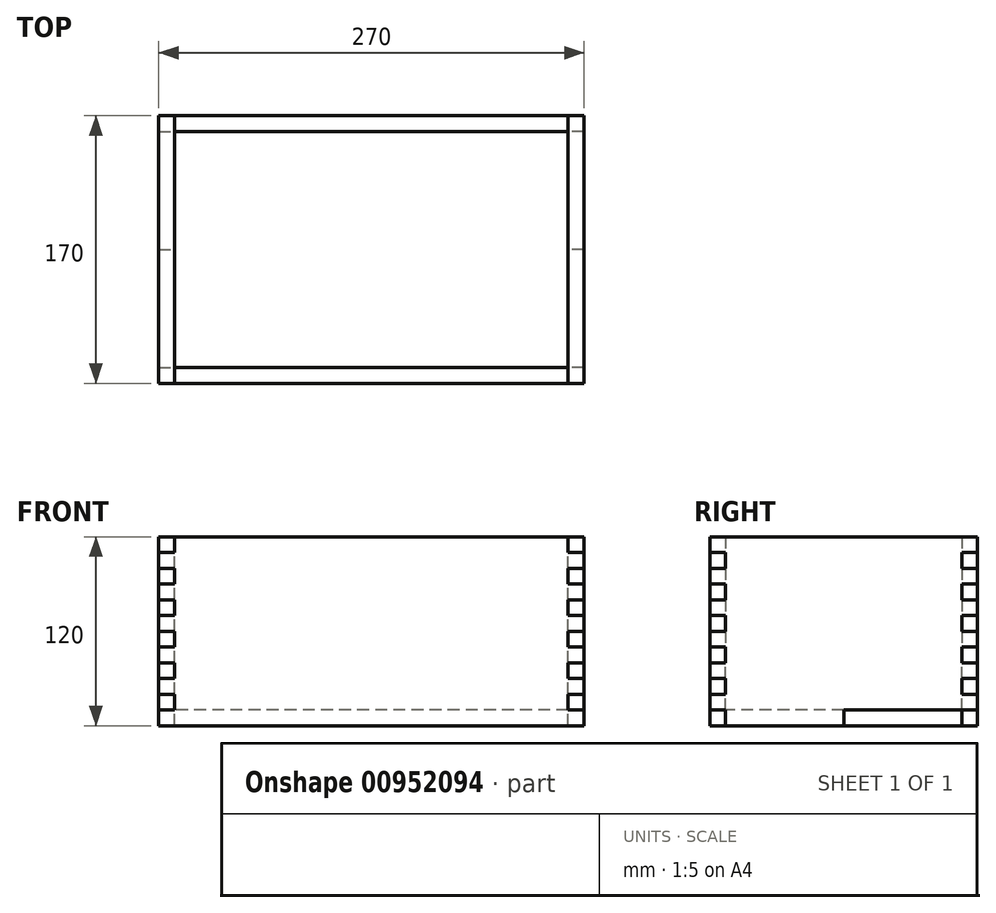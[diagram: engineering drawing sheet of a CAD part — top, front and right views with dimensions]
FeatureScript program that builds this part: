
annotation { "Feature Type Name" : "Feature", "Feature Type Description" : "" }
export const myFeature = defineFeature(function(context is Context, id is Id, definition is map)
    precondition{}
    {
        {
            var Q0;
            Q0=qCreatedBy(makeId("Top.planeOp"),FACE);
            var sketch = newSketch(context, id + "F0", { "sketchPlane" : qUnion([Q0])});
            skLineSegment(sketch, "E0.bottom", {"start": v(125, 75) * mm, "end": v(-125, 75) * mm});
            skLineSegment(sketch, "E0.top", {"start": v(125, -75) * mm, "end": v(-125, -75) * mm});
            skLineSegment(sketch, "E0.left", {"start": v(125, 75) * mm, "end": v(125, -75) * mm});
            skLineSegment(sketch, "E0.right", {"start": v(-125, 75) * mm, "end": v(-125, -75) * mm});
            skPoint(sketch, "E0.middle", {"position": v(0, 0) * mm});
            skSolve(sketch);
        }
        {
            var Q0;
            Q0 = qSketchRegion(id + "F0", true);
            extrude(context, id + "F1", {"entities" : qUnion([Q0]), "depth" : 10 * mm, "offsetDistance" : 25 * mm});
        }
        {
            var Q0;
            Q0=makeQuery(id+"F1.opExtrude","SWEPT_FACE",FACE,{"disambiguationData":[OSD([sQuery(id+"F0.wireOp",EDGE,"E0.right")])]});
            var sketch = newSketch(context, id + "F2", { "sketchPlane" : qUnion([Q0])});
            skLineSegment(sketch, "E1.bottom", {"start": v(0, 0) * mm, "end": v(75, 0) * mm});
            skLineSegment(sketch, "E1.right", {"start": v(85, 10) * mm, "end": v(85, 20) * mm});
            skLineSegment(sketch, "E2.0", {"start": v(75, 0) * mm, "end": v(75, 10) * mm});
            skLineSegment(sketch, "E3", {"start": v(85, 10) * mm, "end": v(75, 10) * mm});
            skLineSegment(sketch, "E4.0.1.0", {"start": v(85, 20) * mm, "end": v(75, 20) * mm});
            skLineSegment(sketch, "E4.0.2.0", {"start": v(85, 30) * mm, "end": v(75, 30) * mm});
            skLineSegment(sketch, "E4.0.3.0", {"start": v(85, 40) * mm, "end": v(75, 40) * mm});
            skLineSegment(sketch, "E4.0.4.0", {"start": v(85, 50) * mm, "end": v(75, 50) * mm});
            skLineSegment(sketch, "E4.0.5.0", {"start": v(85, 60) * mm, "end": v(75, 60) * mm});
            skLineSegment(sketch, "E4.0.6.0", {"start": v(85, 70) * mm, "end": v(75, 70) * mm});
            skLineSegment(sketch, "E4.0.7.0", {"start": v(85, 80) * mm, "end": v(75, 80) * mm});
            skLineSegment(sketch, "E4.0.8.0", {"start": v(85, 90) * mm, "end": v(75, 90) * mm});
            skLineSegment(sketch, "E4.0.9.0", {"start": v(85, 100) * mm, "end": v(75, 100) * mm});
            skLineSegment(sketch, "E4.0.10.0", {"start": v(85, 110) * mm, "end": v(75, 110) * mm});
            skLineSegment(sketch, "E4.0.11.0", {"start": v(85, 120) * mm, "end": v(75, 120) * mm});
            skLineSegment(sketch, "E4.direction1", {"start": v(75, 10) * mm, "end": v(100, 10) * mm, "construction": true});
            skLineSegment(sketch, "E5.trimOffspring", {"start": v(75, 20) * mm, "end": v(75, 30) * mm});
            skLineSegment(sketch, "E6.trimOffspring", {"start": v(85, 30) * mm, "end": v(85, 40) * mm});
            skLineSegment(sketch, "E7.trimOffspring", {"start": v(75, 40) * mm, "end": v(75, 50) * mm});
            skLineSegment(sketch, "E8.trimOffspring", {"start": v(85, 50) * mm, "end": v(85, 60) * mm});
            skLineSegment(sketch, "E9.trimOffspring", {"start": v(75, 60) * mm, "end": v(75, 70) * mm});
            skLineSegment(sketch, "E10.trimOffspring", {"start": v(85, 70) * mm, "end": v(85, 80) * mm});
            skLineSegment(sketch, "E11.trimOffspring", {"start": v(75, 80) * mm, "end": v(75, 90) * mm});
            skLineSegment(sketch, "E12.trimOffspring", {"start": v(85, 90) * mm, "end": v(85, 100) * mm});
            skLineSegment(sketch, "E13.trimOffspring", {"start": v(75, 100) * mm, "end": v(75, 110) * mm});
            skLineSegment(sketch, "E14.trimOffspring", {"start": v(85, 110) * mm, "end": v(85, 120) * mm});
            skLineSegment(sketch, "E15", {"start": v(0, 0) * mm, "end": v(0, 119.51) * mm});
            skLineSegment(sketch, "E16.MirrorCS", {"start": v(-85, 10) * mm, "end": v(-75, 10) * mm});
            skLineSegment(sketch, "E17.MirrorCS", {"start": v(-85, 30) * mm, "end": v(-75, 30) * mm});
            skLineSegment(sketch, "E18.MirrorCS", {"start": v(-85, 110) * mm, "end": v(-75, 110) * mm});
            skLineSegment(sketch, "E19.MirrorCS", {"start": v(-85, 20) * mm, "end": v(-75, 20) * mm});
            skLineSegment(sketch, "E20.MirrorCS", {"start": v(-85, 80) * mm, "end": v(-75, 80) * mm});
            skLineSegment(sketch, "E21.MirrorCS", {"start": v(-75, 60) * mm, "end": v(-75, 70) * mm});
            skLineSegment(sketch, "E22.MirrorCS", {"start": v(-85, 30) * mm, "end": v(-85, 40) * mm});
            skLineSegment(sketch, "E23.MirrorCS", {"start": v(-75, 10) * mm, "end": v(-100, 10) * mm, "construction": true});
            skLineSegment(sketch, "E24.MirrorCS", {"start": v(-85, 50) * mm, "end": v(-75, 50) * mm});
            skLineSegment(sketch, "E25.MirrorCS", {"start": v(-85, 100) * mm, "end": v(-75, 100) * mm});
            skLineSegment(sketch, "E26.MirrorCS", {"start": v(-85, 120) * mm, "end": v(-75, 120) * mm});
            skLineSegment(sketch, "E27.MirrorCS", {"start": v(-85, 90) * mm, "end": v(-75, 90) * mm});
            skLineSegment(sketch, "E28.MirrorCS", {"start": v(-75, 100) * mm, "end": v(-75, 110) * mm});
            skLineSegment(sketch, "E29.MirrorCS", {"start": v(-85, 40) * mm, "end": v(-75, 40) * mm});
            skLineSegment(sketch, "E30.MirrorCS", {"start": v(-85, 110) * mm, "end": v(-85, 120) * mm});
            skLineSegment(sketch, "E31.MirrorCS", {"start": v(-75, 0) * mm, "end": v(-75, 10) * mm});
            skLineSegment(sketch, "E32.MirrorCS", {"start": v(-75, 40) * mm, "end": v(-75, 50) * mm});
            skLineSegment(sketch, "E33.MirrorCS", {"start": v(-75, 80) * mm, "end": v(-75, 90) * mm});
            skLineSegment(sketch, "E34.MirrorCS", {"start": v(-85, 70) * mm, "end": v(-75, 70) * mm});
            skLineSegment(sketch, "E35.MirrorCS", {"start": v(-85, 70) * mm, "end": v(-85, 80) * mm});
            skLineSegment(sketch, "E36.MirrorCS", {"start": v(-75, 20) * mm, "end": v(-75, 30) * mm});
            skLineSegment(sketch, "E37.MirrorCS", {"start": v(-85, 60) * mm, "end": v(-75, 60) * mm});
            skLineSegment(sketch, "E38.MirrorCS", {"start": v(-85, 90) * mm, "end": v(-85, 100) * mm});
            skLineSegment(sketch, "E39.MirrorCS", {"start": v(-85, 50) * mm, "end": v(-85, 60) * mm});
            skLineSegment(sketch, "E40.MirrorCS", {"start": v(0, 0) * mm, "end": v(-75, 0) * mm});
            skLineSegment(sketch, "E41.MirrorCS", {"start": v(-85, 10) * mm, "end": v(-85, 20) * mm});
            skLineSegment(sketch, "E42", {"start": v(-75, 10) * mm, "end": v(-75, 0) * mm});
            skLineSegment(sketch, "E43", {"start": v(-75, 0) * mm, "end": v(75, 0) * mm});
            skLineSegment(sketch, "E44", {"start": v(75, 120) * mm, "end": v(-75, 120) * mm});
            skSolve(sketch);
        }
        {
            var Q0;
            {var subQ0=sQuery(id+"F2.wireOp",EDGE,"E16.MirrorCS");Q0=makeQuery(id+"F2.imprint","IMPRINT",FACE,{"disambiguationData":[TD([[makeQuery(id+"F2.imprint","IMPRINT",EDGE,{"derivedFrom":subQ0}),1.0]])]});}
            var Q1;
            {var subQ4=sQuery(id+"F2.wireOp",EDGE,"E1.top");Q1=makeQuery(id+"F2.imprint","IMPRINT",FACE,{"disambiguationData":[TD([[makeQuery(id+"F2.imprint","IMPRINT",EDGE,{"derivedFrom":subQ4}),-1.0]])]});}
            var Q2;
            {var subQ5=sQuery(id+"F2.wireOp",EDGE,"E42");Q2=makeQuery(id+"F2.imprint","IMPRINT",FACE,{"disambiguationData":[TD([[makeQuery(id+"F2.imprint","IMPRINT",EDGE,{"derivedFrom":subQ5}),1.0]])]});}
            var Q3;
            {var subQ5=sQuery(id+"F2.wireOp",EDGE,"E2.0");Q3=makeQuery(id+"F2.imprint","IMPRINT",FACE,{"disambiguationData":[TD([[makeQuery(id+"F2.imprint","IMPRINT",EDGE,{"derivedFrom":subQ5}),-1.0]])]});}
            extrude(context, id + "F3", {"entities" : qUnion([Q0, Q1, Q2, Q3]), "depth" : 10 * mm, "offsetDistance" : 25 * mm});
        }
        {
            var Q0;
            Q0=makeQuery(id+"F3.opExtrude","SWEPT_BODY",BODY,{"disambiguationData":[OSD([sQuery(id+"F2.wireOp",EDGE,"E1.top"),sQuery(id+"F2.wireOp",EDGE,"E1.right"),sQuery(id+"F2.wireOp",EDGE,"E3"),sQuery(id+"F2.wireOp",EDGE,"E4.0.1.0"),sQuery(id+"F2.wireOp",EDGE,"E4.0.2.0"),sQuery(id+"F2.wireOp",EDGE,"E4.0.3.0"),sQuery(id+"F2.wireOp",EDGE,"E4.0.4.0"),sQuery(id+"F2.wireOp",EDGE,"E4.0.5.0"),sQuery(id+"F2.wireOp",EDGE,"E4.0.6.0"),sQuery(id+"F2.wireOp",EDGE,"E4.0.7.0"),sQuery(id+"F2.wireOp",EDGE,"E4.0.8.0"),sQuery(id+"F2.wireOp",EDGE,"E4.0.9.0"),sQuery(id+"F2.wireOp",EDGE,"E4.0.10.0"),sQuery(id+"F2.wireOp",EDGE,"E4.0.11.0"),sQuery(id+"F2.wireOp",EDGE,"E4.0.12.0"),sQuery(id+"F2.wireOp",EDGE,"537c9ae5-ac88-4067-9cdc-c8666f4d1ff7.0.0.13"),sQuery(id+"F2.wireOp",EDGE,"E5.trimOffspring"),sQuery(id+"F2.wireOp",EDGE,"E6.trimOffspring"),sQuery(id+"F2.wireOp",EDGE,"E7.trimOffspring"),sQuery(id+"F2.wireOp",EDGE,"E8.trimOffspring"),sQuery(id+"F2.wireOp",EDGE,"E9.trimOffspring"),sQuery(id+"F2.wireOp",EDGE,"E10.trimOffspring"),sQuery(id+"F2.wireOp",EDGE,"E11.trimOffspring"),sQuery(id+"F2.wireOp",EDGE,"E12.trimOffspring"),sQuery(id+"F2.wireOp",EDGE,"E13.trimOffspring"),sQuery(id+"F2.wireOp",EDGE,"E14.trimOffspring"),sQuery(id+"F2.wireOp",EDGE,"0b9fcc7d-6960-4033-8808-0068f41279c2.trimOffspring"),sQuery(id+"F2.wireOp",EDGE,"4482ad7b-3059-4b9f-bfc4-0e486806ed4d.trimOffspring"),sQuery(id+"F2.wireOp",EDGE,"a6469687-5e93-42e0-971b-389a09a8f158.trimOffspring"),sQuery(id+"F2.wireOp",EDGE,"E16.MirrorCS"),sQuery(id+"F2.wireOp",EDGE,"E17.MirrorCS"),sQuery(id+"F2.wireOp",EDGE,"e481a68e-a1f5-484a-a6b3-999f8e45b44d3.MirrorCS"),sQuery(id+"F2.wireOp",EDGE,"E18.MirrorCS"),sQuery(id+"F2.wireOp",EDGE,"E19.MirrorCS"),sQuery(id+"F2.wireOp",EDGE,"E20.MirrorCS"),sQuery(id+"F2.wireOp",EDGE,"E21.MirrorCS"),sQuery(id+"F2.wireOp",EDGE,"E22.MirrorCS"),sQuery(id+"F2.wireOp",EDGE,"e481a68e-a1f5-484a-a6b3-999f8e45b44d9.MirrorCS"),sQuery(id+"F2.wireOp",EDGE,"E24.MirrorCS"),sQuery(id+"F2.wireOp",EDGE,"e481a68e-a1f5-484a-a6b3-999f8e45b44d12.MirrorCS"),sQuery(id+"F2.wireOp",EDGE,"E25.MirrorCS"),sQuery(id+"F2.wireOp",EDGE,"E26.MirrorCS"),sQuery(id+"F2.wireOp",EDGE,"E27.MirrorCS"),sQuery(id+"F2.wireOp",EDGE,"E28.MirrorCS"),sQuery(id+"F2.wireOp",EDGE,"E29.MirrorCS"),sQuery(id+"F2.wireOp",EDGE,"e481a68e-a1f5-484a-a6b3-999f8e45b44d18.MirrorCS"),sQuery(id+"F2.wireOp",EDGE,"E30.MirrorCS"),sQuery(id+"F2.wireOp",EDGE,"E32.MirrorCS"),sQuery(id+"F2.wireOp",EDGE,"E33.MirrorCS"),sQuery(id+"F2.wireOp",EDGE,"E34.MirrorCS"),sQuery(id+"F2.wireOp",EDGE,"E35.MirrorCS"),sQuery(id+"F2.wireOp",EDGE,"E36.MirrorCS"),sQuery(id+"F2.wireOp",EDGE,"E37.MirrorCS"),sQuery(id+"F2.wireOp",EDGE,"E38.MirrorCS"),sQuery(id+"F2.wireOp",EDGE,"E178.MirrorCS"),sQuery(id+"F2.wireOp",EDGE,"E39.MirrorCS"),sQuery(id+"F2.wireOp",EDGE,"E41.MirrorCS"),sQuery(id+"F2.wireOp",EDGE,"e481a68e-a1f5-484a-a6b3-999f8e45b44d32.MirrorCS"),sQuery(id+"F2.wireOp",EDGE,"E42"),sQuery(id+"F2.wireOp",EDGE,"E43"),sQuery(id+"F2.wireOp",EDGE,"E2.0")])]});
            var Q1;
            Q1=qCreatedBy(makeId("Right.planeOp"),FACE);
            mirror(context, id + "F4", {"entities" : qUnion([Q0]), "mirrorPlane" : qUnion([Q1])});
        }
        {
            var Q0;
            Q0=makeQuery(id+"F1.opExtrude","SWEPT_FACE",FACE,{"disambiguationData":[OSD([sQuery(id+"F0.wireOp",EDGE,"E0.bottom")])]});
            var sketch = newSketch(context, id + "F5", { "sketchPlane" : qUnion([Q0])});
            skLineSegment(sketch, "E45", {"start": v(0, 0) * mm, "end": v(135, 0) * mm});
            skLineSegment(sketch, "E46", {"start": v(135, 0) * mm, "end": v(135, 10) * mm});
            skLineSegment(sketch, "E47", {"start": v(135, 10) * mm, "end": v(125, 10) * mm});
            skLineSegment(sketch, "E48", {"start": v(125, 10) * mm, "end": v(125, 20) * mm});
            skLineSegment(sketch, "E49", {"start": v(125, 20) * mm, "end": v(135, 20) * mm});
            skLineSegment(sketch, "E50", {"start": v(135, 20) * mm, "end": v(135, 30) * mm});
            skLineSegment(sketch, "E51", {"start": v(135, 30) * mm, "end": v(125, 30) * mm});
            skLineSegment(sketch, "E52", {"start": v(125, 30) * mm, "end": v(125, 40) * mm});
            skLineSegment(sketch, "E53", {"start": v(125, 40) * mm, "end": v(135, 40) * mm});
            skLineSegment(sketch, "E54.0.1.0", {"start": v(125, 50) * mm, "end": v(135, 50) * mm});
            skLineSegment(sketch, "E54.0.2.0", {"start": v(125, 60) * mm, "end": v(135, 60) * mm});
            skLineSegment(sketch, "E54.0.3.0", {"start": v(125, 70) * mm, "end": v(135, 70) * mm});
            skLineSegment(sketch, "E54.0.4.0", {"start": v(125, 80) * mm, "end": v(135, 80) * mm});
            skLineSegment(sketch, "E54.0.5.0", {"start": v(125, 90) * mm, "end": v(135, 90) * mm});
            skLineSegment(sketch, "E54.0.6.0", {"start": v(125, 100) * mm, "end": v(135, 100) * mm});
            skLineSegment(sketch, "E54.0.7.0", {"start": v(125, 110) * mm, "end": v(135, 110) * mm});
            skLineSegment(sketch, "E54.0.8.0", {"start": v(125, 120) * mm, "end": v(135, 120) * mm});
            skLineSegment(sketch, "E54.direction1", {"start": v(125, 40) * mm, "end": v(150, 40) * mm, "construction": true});
            skLineSegment(sketch, "E54.direction2", {"start": v(125, 40) * mm, "end": v(125, 50) * mm, "construction": true});
            skLineSegment(sketch, "E55", {"start": v(135, 50) * mm, "end": v(135, 40) * mm});
            skLineSegment(sketch, "E56", {"start": v(125, 60) * mm, "end": v(125, 50) * mm});
            skLineSegment(sketch, "E57", {"start": v(135, 70) * mm, "end": v(135, 60) * mm});
            skLineSegment(sketch, "E58", {"start": v(125, 80) * mm, "end": v(125, 70) * mm});
            skLineSegment(sketch, "E59", {"start": v(135, 90) * mm, "end": v(135, 80) * mm});
            skLineSegment(sketch, "E60", {"start": v(125, 100) * mm, "end": v(125, 90) * mm});
            skLineSegment(sketch, "E61", {"start": v(135, 110) * mm, "end": v(135, 100) * mm});
            skLineSegment(sketch, "E62", {"start": v(125, 120) * mm, "end": v(125, 110) * mm});
            skLineSegment(sketch, "E63", {"start": v(0, 120) * mm, "end": v(0, 0) * mm});
            skLineSegment(sketch, "E64.MirrorCS", {"start": v(-125, 40) * mm, "end": v(-135, 40) * mm});
            skLineSegment(sketch, "E65.MirrorCS", {"start": v(-125, 40) * mm, "end": v(-150, 40) * mm, "construction": true});
            skLineSegment(sketch, "E66.MirrorCS", {"start": v(-125, 120) * mm, "end": v(-135, 120) * mm});
            skLineSegment(sketch, "E67.MirrorCS", {"start": v(-125, 80) * mm, "end": v(-135, 80) * mm});
            skLineSegment(sketch, "E68.MirrorCS", {"start": v(-135, 30) * mm, "end": v(-125, 30) * mm});
            skLineSegment(sketch, "E69.MirrorCS", {"start": v(-125, 50) * mm, "end": v(-135, 50) * mm});
            skLineSegment(sketch, "E70.MirrorCS", {"start": v(-125, 40) * mm, "end": v(-125, 50) * mm, "construction": true});
            skLineSegment(sketch, "E71.MirrorCS", {"start": v(-135, 110) * mm, "end": v(-135, 100) * mm});
            skLineSegment(sketch, "E72.MirrorCS", {"start": v(-125, 60) * mm, "end": v(-135, 60) * mm});
            skLineSegment(sketch, "E73.MirrorCS", {"start": v(-125, 20) * mm, "end": v(-135, 20) * mm});
            skLineSegment(sketch, "E74.MirrorCS", {"start": v(-125, 110) * mm, "end": v(-135, 110) * mm});
            skLineSegment(sketch, "E75.MirrorCS", {"start": v(-135, 90) * mm, "end": v(-135, 80) * mm});
            skLineSegment(sketch, "E76.MirrorCS", {"start": v(-135, 70) * mm, "end": v(-135, 60) * mm});
            skLineSegment(sketch, "E77.MirrorCS", {"start": v(-135, 10) * mm, "end": v(-125, 10) * mm});
            skLineSegment(sketch, "E78.MirrorCS", {"start": v(-135, 0) * mm, "end": v(-135, 10) * mm});
            skLineSegment(sketch, "E79.MirrorCS", {"start": v(-125, 30) * mm, "end": v(-125, 40) * mm});
            skLineSegment(sketch, "E80.MirrorCS", {"start": v(-125, 80) * mm, "end": v(-125, 70) * mm});
            skLineSegment(sketch, "E81.MirrorCS", {"start": v(-125, 100) * mm, "end": v(-125, 90) * mm});
            skLineSegment(sketch, "E82.MirrorCS", {"start": v(-135, 50) * mm, "end": v(-135, 40) * mm});
            skLineSegment(sketch, "E83.MirrorCS", {"start": v(-125, 60) * mm, "end": v(-125, 50) * mm});
            skLineSegment(sketch, "E84.MirrorCS", {"start": v(-125, 120) * mm, "end": v(-125, 110) * mm});
            skLineSegment(sketch, "E85.MirrorCS", {"start": v(-125, 100) * mm, "end": v(-135, 100) * mm});
            skLineSegment(sketch, "E86.MirrorCS", {"start": v(-125, 90) * mm, "end": v(-135, 90) * mm});
            skLineSegment(sketch, "E87.MirrorCS", {"start": v(-125, 10) * mm, "end": v(-125, 20) * mm});
            skLineSegment(sketch, "E88.MirrorCS", {"start": v(-125, 70) * mm, "end": v(-135, 70) * mm});
            skLineSegment(sketch, "E89.MirrorCS", {"start": v(-135, 20) * mm, "end": v(-135, 30) * mm});
            skLineSegment(sketch, "E90.MirrorCS", {"start": v(0, 0) * mm, "end": v(-135, 0) * mm});
            skLineSegment(sketch, "E91", {"start": v(-125, 120) * mm, "end": v(125, 120) * mm});
            skSolve(sketch);
        }
        {
            var Q0;
            Q0=makeQuery(id+"F5.imprint","IMPRINT",FACE,{"disambiguationData":[TD([[makeQuery(id+"F5.imprint","IMPRINT",EDGE,{"derivedFrom":sQuery(id+"F5.wireOp",EDGE,"E64.MirrorCS")}),-1.0]])]});
            var Q1;
            {var subQ0=sQuery(id+"F5.wireOp",EDGE,"E48");Q1=makeQuery(id+"F5.imprint","IMPRINT",FACE,{"disambiguationData":[TD([[makeQuery(id+"F5.imprint","IMPRINT",EDGE,{"derivedFrom":subQ0}),1.0]])]});}
            var Q2;
            {var subQ3=sQuery(id+"F0.wireOp",EDGE,"E0.bottom");var subQ6=makeQuery(id+"F1.opExtrude","SWEPT_EDGE",EDGE,{"disambiguationData":[OSD([subQ3,sQuery(id+"F0.wireOp",EDGE,"E0.left")])]});Q2=makeQuery(id+"F5.imprint","IMPRINT",FACE,{"disambiguationData":[TD([[makeQuery(id+"F5.imprint","IMPRINT",EDGE,{"derivedFrom":subQ6}),1.0]])]});}
            var Q3;
            {var subQ1=sQuery(id+"F0.wireOp",EDGE,"E0.bottom");var subQ2=makeQuery(id+"F1.opExtrude","SWEPT_EDGE",EDGE,{"disambiguationData":[OSD([subQ1,sQuery(id+"F0.wireOp",EDGE,"E0.right")])]});Q3=makeQuery(id+"F5.imprint","IMPRINT",FACE,{"disambiguationData":[TD([[makeQuery(id+"F5.imprint","IMPRINT",EDGE,{"derivedFrom":subQ2}),-1.0]])]});}
            var Q4;
            {var subQ2=sQuery(id+"F5.wireOp",EDGE,"E46");Q4=makeQuery(id+"F5.imprint","IMPRINT",FACE,{"disambiguationData":[TD([[makeQuery(id+"F5.imprint","IMPRINT",EDGE,{"derivedFrom":subQ2}),1.0]])]});}
            var Q5;
            Q5=makeQuery(id+"F5.imprint","IMPRINT",FACE,{"disambiguationData":[TD([[makeQuery(id+"F5.imprint","IMPRINT",EDGE,{"derivedFrom":sQuery(id+"F5.wireOp",EDGE,"E77.MirrorCS")}),-1.0]])]});
            extrude(context, id + "F6", {"entities" : qUnion([Q0, Q1, Q2, Q3, Q4, Q5]), "depth" : 10 * mm, "offsetDistance" : 25 * mm});
        }
        {
            var Q0;
            Q0=makeQuery(id+"F6.opExtrude","SWEPT_BODY",BODY,{"disambiguationData":[OSD([sQuery(id+"F5.wireOp",EDGE,"E45"),sQuery(id+"F5.wireOp",EDGE,"E46"),sQuery(id+"F5.wireOp",EDGE,"E47"),sQuery(id+"F5.wireOp",EDGE,"E48"),sQuery(id+"F5.wireOp",EDGE,"E49"),sQuery(id+"F5.wireOp",EDGE,"E50"),sQuery(id+"F5.wireOp",EDGE,"E51"),sQuery(id+"F5.wireOp",EDGE,"E52"),sQuery(id+"F5.wireOp",EDGE,"E53"),sQuery(id+"F5.wireOp",EDGE,"E54.0.1.0"),sQuery(id+"F5.wireOp",EDGE,"E54.0.2.0"),sQuery(id+"F5.wireOp",EDGE,"E54.0.3.0"),sQuery(id+"F5.wireOp",EDGE,"E54.0.4.0"),sQuery(id+"F5.wireOp",EDGE,"E54.0.5.0"),sQuery(id+"F5.wireOp",EDGE,"E54.0.6.0"),sQuery(id+"F5.wireOp",EDGE,"E54.0.7.0"),sQuery(id+"F5.wireOp",EDGE,"E54.0.8.0"),sQuery(id+"F5.wireOp",EDGE,"E54.0.9.0"),sQuery(id+"F5.wireOp",EDGE,"E54.0.10.0"),sQuery(id+"F5.wireOp",EDGE,"E55"),sQuery(id+"F5.wireOp",EDGE,"E56"),sQuery(id+"F5.wireOp",EDGE,"E57"),sQuery(id+"F5.wireOp",EDGE,"E58"),sQuery(id+"F5.wireOp",EDGE,"E59"),sQuery(id+"F5.wireOp",EDGE,"E60"),sQuery(id+"F5.wireOp",EDGE,"E61"),sQuery(id+"F5.wireOp",EDGE,"E62"),sQuery(id+"F5.wireOp",EDGE,"BKastwjj-v0CP-P6UC-iaaF-gybE2uktd5xK"),sQuery(id+"F5.wireOp",EDGE,"IMumOhdv-rOUg-QHwQ-wN91-30HeblFpbXj6"),sQuery(id+"F5.wireOp",EDGE,"H1P5XP6w-vSr6-V5xl-ufny-EVKaZelg01Pk"),sQuery(id+"F5.wireOp",EDGE,"jXIq9f07-MvTq-TXnW-k20t-MuA2jao6ik3o"),sQuery(id+"F5.wireOp",EDGE,"E64.MirrorCS"),sQuery(id+"F5.wireOp",EDGE,"07780a3d-623b-4ada-b590-cf2055f8bb8e1.MirrorCS"),sQuery(id+"F5.wireOp",EDGE,"E68.MirrorCS"),sQuery(id+"F5.wireOp",EDGE,"07780a3d-623b-4ada-b590-cf2055f8bb8e3.MirrorCS"),sQuery(id+"F5.wireOp",EDGE,"07780a3d-623b-4ada-b590-cf2055f8bb8e5.MirrorCS"),sQuery(id+"F5.wireOp",EDGE,"E89.MirrorCS"),sQuery(id+"F5.wireOp",EDGE,"07780a3d-623b-4ada-b590-cf2055f8bb8e8.MirrorCS"),sQuery(id+"F5.wireOp",EDGE,"E73.MirrorCS"),sQuery(id+"F5.wireOp",EDGE,"E82.MirrorCS"),sQuery(id+"F5.wireOp",EDGE,"07780a3d-623b-4ada-b590-cf2055f8bb8e11.MirrorCS"),sQuery(id+"F5.wireOp",EDGE,"E87.MirrorCS"),sQuery(id+"F5.wireOp",EDGE,"E77.MirrorCS"),sQuery(id+"F5.wireOp",EDGE,"E78.MirrorCS"),sQuery(id+"F5.wireOp",EDGE,"E90.MirrorCS"),sQuery(id+"F5.wireOp",EDGE,"07780a3d-623b-4ada-b590-cf2055f8bb8e16.MirrorCS"),sQuery(id+"F5.wireOp",EDGE,"E75.MirrorCS"),sQuery(id+"F5.wireOp",EDGE,"E83.MirrorCS"),sQuery(id+"F5.wireOp",EDGE,"E76.MirrorCS"),sQuery(id+"F5.wireOp",EDGE,"E69.MirrorCS"),sQuery(id+"F5.wireOp",EDGE,"E74.MirrorCS"),sQuery(id+"F5.wireOp",EDGE,"E80.MirrorCS"),sQuery(id+"F5.wireOp",EDGE,"E66.MirrorCS"),sQuery(id+"F5.wireOp",EDGE,"E84.MirrorCS"),sQuery(id+"F5.wireOp",EDGE,"E81.MirrorCS"),sQuery(id+"F5.wireOp",EDGE,"E88.MirrorCS"),sQuery(id+"F5.wireOp",EDGE,"E67.MirrorCS"),sQuery(id+"F5.wireOp",EDGE,"E86.MirrorCS"),sQuery(id+"F5.wireOp",EDGE,"E85.MirrorCS"),sQuery(id+"F5.wireOp",EDGE,"E79.MirrorCS"),sQuery(id+"F5.wireOp",EDGE,"E71.MirrorCS"),sQuery(id+"F5.wireOp",EDGE,"E72.MirrorCS")])]});
            var Q1;
            Q1=qCreatedBy(makeId("Front.planeOp"),FACE);
            mirror(context, id + "F7", {"entities" : qUnion([Q0]), "mirrorPlane" : qUnion([Q1])});
        }
    });
